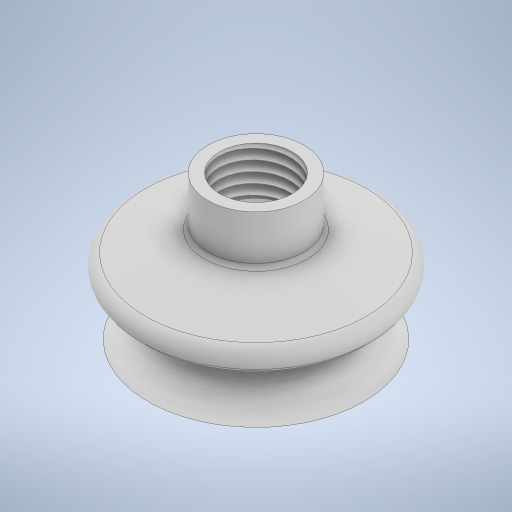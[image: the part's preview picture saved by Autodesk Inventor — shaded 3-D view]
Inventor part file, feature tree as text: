
AUTODESK INVENTOR PART (.ipt)
format: ipt  version: 2024 (Build 280153000, 153)  size: 359,936 bytes
history: native  units: mm
features: extrude x3, fillet x3, chamfer x2, other x1, revolve x1, hole x1, sketch x1
ambient origin geometry x8: Origin, YZ Plane, XZ Plane, XY Plane, X Axis, Y Axis, Z Axis, Center Point
bodies: Body1 (feature_tree)
feature tree (12):
  other  "Sólido1"
  extrude  "Extrusión1"  Depth=10.0mm TaperAngle=0.0deg
  extrude  "Extrusión2"  Depth=1.0mm
  extrude  "Extrusión3"  Depth=10.0mm TaperAngle=0.0deg
  chamfer  "Chaflán1"  Distance=20.0mm
  chamfer  "Chaflán2"  Distance=10.0mm
  fillet  "Empalme1"  Radius=15.0mm
  revolve  "Revolución1"  Angle=45.0deg
  fillet  "Empalme2"  Radius=2.5mm
  hole  "Agujero1"  [1 undecoded]
  fillet  "Empalme3"  [1 undecoded]
  sketch  "Boceto5"  dims[d0=45.0mm d1=10.0mm d2=0.0mm d3=50.0mm d4=10.0mm d5=0.0mm d6=20.0mm d7=10.0mm d8=0.0mm d9=15.0mm d10=5.0mm d11=45.0deg d12=2.5mm d13=7.75mm d14=45.0deg d15=2.5mm d16=5.0mm d17=90.0deg d18=2.0mm d19=15.1638mm d20=10.0mm d21=4.0mm d22=2.0mm d23=90.0deg d24=8.0mm d25=20.594885mm d26=1.0mm]
note: 2 required parameter values undecoded (feature->parameter linkage not recoverable at this tier; creation-order binding heuristic only, values carry confidence <= 0.55)
